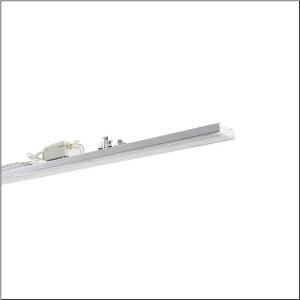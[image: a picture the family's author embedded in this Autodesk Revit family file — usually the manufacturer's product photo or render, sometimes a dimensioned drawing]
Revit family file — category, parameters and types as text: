
# Revit family: licross_11_recessed_ho_51te11mn4exs
name_source: partatom
category: Lighting Fixtures
units: mm (PartAtom-declared; Revit-internal decimal feet)

## family parameters
Cut with Voids When Loaded = No
Host = Face
Light Source = No
Part Type = Normal
Room Calculation Point = No
Round Connector Dimension = Use Diameter
Shared = No

## types (1)
- --- (1 x LED, 14070 lm, 74.5 W, 4000K)
    Apparent Load = 75 VA
    CIE Flux Codes = 87 95 99 100 100
    Color Rendering = 80
    Color Temperature = 4000K
    Default Elevation = 1800 mm
    Description = Licross 11 Recessed HO, luminaire insert, of sheet steel, galvanised, coil coated, white, length: 1.500mm, width: 66mm, height: 67mm, LED rated luminous flux: 14.070lm, light colour: 840, SDCM (Standard Deviation of Colour Matching)MacAdam ≤ 2 SDCM (initial), control gear: ON/OFF Multilumen, with plug, 3-pole, with phase selection, mains connection: 220..240V, AC, 50/60Hz, rated input power: 75W, internal wiring halogen-free, primary light control with lens, of plastic, primary optical cover: cover, of PMMA, light emission: direct distribution, primary light characteristic: symmetric, protection rating (complete): IP54, insulation class (complete): insulation class I (protective earthing), certification: CE, ENEC, VDE, UKCA, protection symbol: D if used in an environment with non-conductive dust loads with corresponding accessories, impact resistance: IK06, permissible ambient temperature for indoor applications: -35..+35°C, corresponds to IFS (International Featured Standards) requirements for safety and quality in the food industry, reducing of maximum allowable ambient temperature of 5°C with ceiling mounting, The light source and the operating device comply with the requirements of the Ecodesign Regulation (EU) 2019/2020 and are replaceable in accordance with this regulation, packaging unit: 1 piece
    Height = 58 mm
    Lamp = 1 x LED
    Lamp Light Flux = 14070 lm
    Lamp Power = 74.5 W
    Lamp count = 1
    Length = 1500 mm
    Luminous efficacy = 189 lm/W
    Manufacturer = Siteco
    ModVariant = No
    Model = 51TE11MN4EXS
    Mounting Place = Ceiling
    Mounting Type = Pendant
    Number of Poles = 1
    OnlyDefault = Yes
    Power Factor = 1
    Product Name = Licross 11 Recessed HO
    Product group = luminaire insert | ceiling pendant
    ProductGroupID = 901
    Protection Class = Protection class I
    Protection Degree = IP 54
    RLX_Detail_Level = 1
    RLX_Emergency_Light_Flux = 0 lm
    RLX_Emergency_Type = 0
    RLX_Emergency_Type_DB = No
    RlxData = <blob elided: 22469 chars, md5=59c3e1e1>
    Socket = socket
    Standby Power = 0 W
    System Light Flux = 14070 lm
    System Power = 75 W
    Type Comments = factory setting: luminous flux: 100 % | (A | C | E) | 174 mA
    Type Image = l_1296930.jpg
    URL = http://relux.com
    VarID = @adj_091039
    Voltage = 0 V
    Weight = 0.00 kg
    Width = 66 mm

## geometry (parser evidence)
native form markers: Blend x4, Sweep x11
no freeform markers — native parametric forms only
